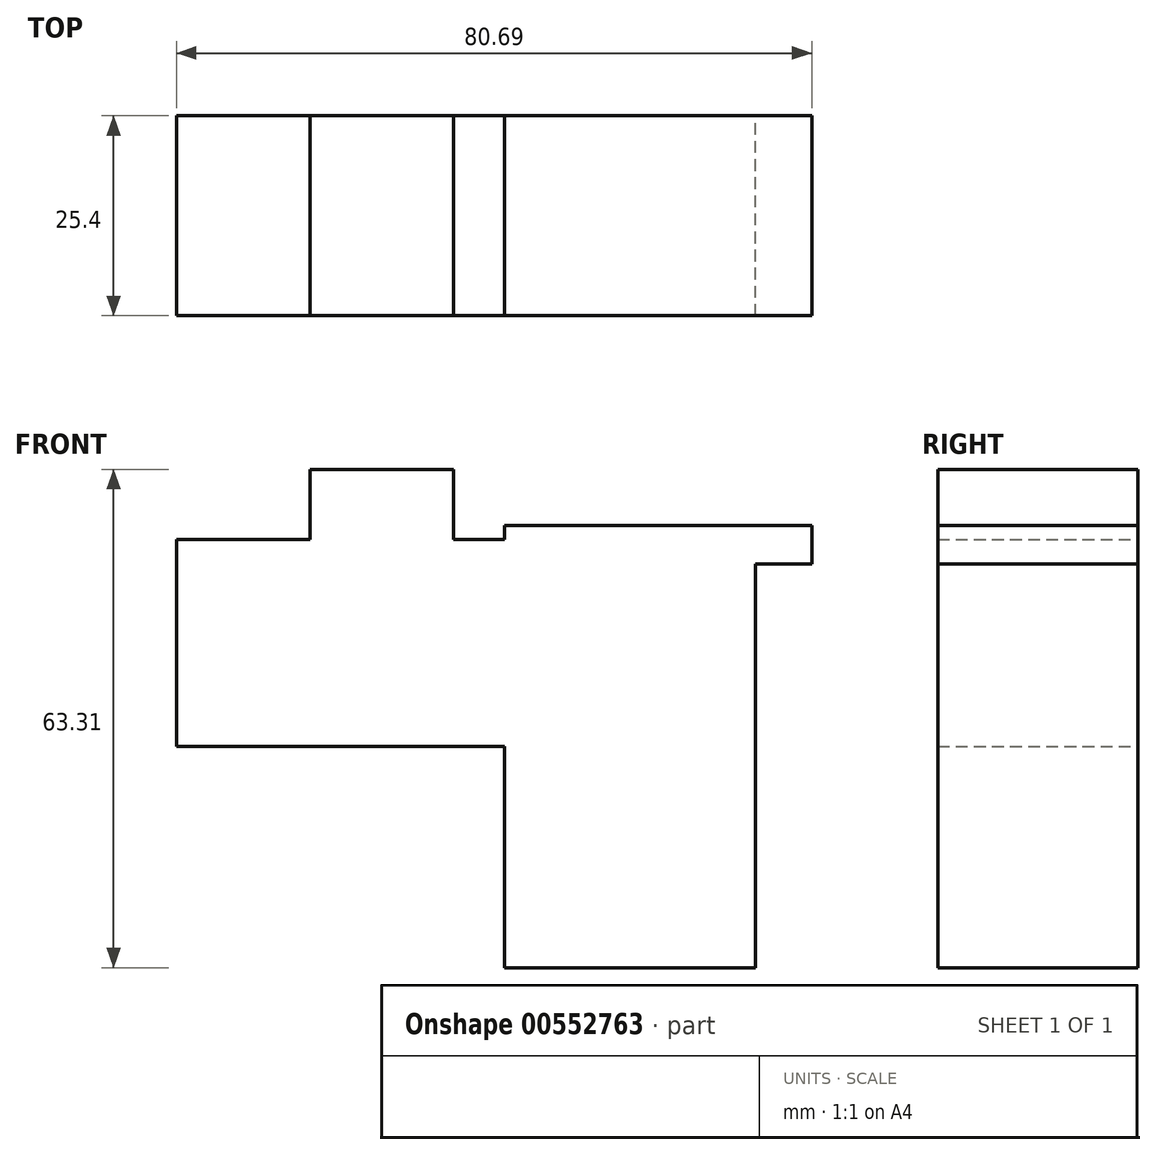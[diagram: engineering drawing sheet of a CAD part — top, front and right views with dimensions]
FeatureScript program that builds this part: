
annotation { "Feature Type Name" : "Feature", "Feature Type Description" : "" }
export const myFeature = defineFeature(function(context is Context, id is Id, definition is map)
    precondition{}
    {
        {
            var Q0;
            Q0=qCreatedBy(makeId("Front.planeOp"),FACE);
            var sketch = newSketch(context, id + "F0", { "sketchPlane" : qUnion([Q0])});
            skLineSegment(sketch, "E0.bottom", {"start": v(0, 0) * mm, "end": v(-41.68, 0) * mm});
            skLineSegment(sketch, "E0.top", {"start": v(0, 26.3) * mm, "end": v(-41.68, 26.3) * mm});
            skLineSegment(sketch, "E0.left", {"start": v(0, 0) * mm, "end": v(0, 26.3) * mm});
            skLineSegment(sketch, "E0.right", {"start": v(-41.68, 0) * mm, "end": v(-41.68, 26.3) * mm});
            skLineSegment(sketch, "E1.bottom", {"start": v(0, 0) * mm, "end": v(31.88, 0) * mm});
            skLineSegment(sketch, "E1.top", {"start": v(0, -28.09) * mm, "end": v(31.88, -28.09) * mm});
            skLineSegment(sketch, "E1.left", {"start": v(0, 0) * mm, "end": v(0, -28.09) * mm});
            skLineSegment(sketch, "E1.right", {"start": v(31.88, 0) * mm, "end": v(31.88, -28.09) * mm});
            skLineSegment(sketch, "E2.top", {"start": v(0, 28.09) * mm, "end": v(31.88, 28.09) * mm});
            skLineSegment(sketch, "E2.left", {"start": v(0, 0) * mm, "end": v(0, 28.09) * mm});
            skLineSegment(sketch, "E2.right", {"start": v(31.88, 0) * mm, "end": v(31.88, 28.09) * mm});
            skLineSegment(sketch, "E3.bottom", {"start": v(-41.68, 0) * mm, "end": v(0, 0) * mm});
            skLineSegment(sketch, "E3.top", {"start": v(-41.68, -28.09) * mm, "end": v(0, -28.09) * mm});
            skLineSegment(sketch, "E3.left", {"start": v(-41.68, 0) * mm, "end": v(-41.68, -28.09) * mm});
            skLineSegment(sketch, "E4.bottom", {"start": v(31.88, 28.09) * mm, "end": v(39, 28.09) * mm});
            skLineSegment(sketch, "E4.top", {"start": v(31.88, 23.18) * mm, "end": v(39, 23.18) * mm});
            skLineSegment(sketch, "E4.left", {"start": v(31.88, 28.09) * mm, "end": v(31.88, 23.18) * mm});
            skLineSegment(sketch, "E4.right", {"start": v(39, 28.09) * mm, "end": v(39, 23.18) * mm});
            skLineSegment(sketch, "E5.bottom", {"start": v(-24.74, 8.02) * mm, "end": v(-6.46, 8.02) * mm});
            skLineSegment(sketch, "E5.top", {"start": v(-24.74, 35.22) * mm, "end": v(-6.46, 35.22) * mm});
            skLineSegment(sketch, "E5.left", {"start": v(-24.74, 8.02) * mm, "end": v(-24.74, 35.22) * mm});
            skLineSegment(sketch, "E5.right", {"start": v(-6.46, 8.02) * mm, "end": v(-6.46, 35.22) * mm});
            skSolve(sketch);
        }
        {
            var Q0;
            {var subQ5=sQuery(id+"F0.wireOp",EDGE,"E5.top");Q0=makeQuery(id+"F0.imprint","IMPRINT",FACE,{"disambiguationData":[TD([[makeQuery(id+"F0.imprint","IMPRINT",EDGE,{"derivedFrom":subQ5}),-1.0]])]});}
            var Q1;
            Q1=makeQuery(id+"F0.imprint","IMPRINT",FACE,{"disambiguationData":[TD([[makeQuery(id+"F0.imprint","IMPRINT",EDGE,{"derivedFrom":sQuery(id+"F0.wireOp",EDGE,"E4.bottom")}),-1.0]])]});
            var Q2;
            {var subQ5=sQuery(id+"F0.wireOp",EDGE,"E5.bottom");Q2=makeQuery(id+"F0.imprint","IMPRINT",FACE,{"disambiguationData":[TD([[makeQuery(id+"F0.imprint","IMPRINT",EDGE,{"derivedFrom":subQ5}),1.0]])]});}
            var Q3;
            Q3=makeQuery(id+"F0.imprint","IMPRINT",FACE,{"disambiguationData":[TD([[makeQuery(id+"F0.imprint","IMPRINT",EDGE,{"derivedFrom":sQuery(id+"F0.wireOp",EDGE,"E3.bottom")}),-1.0]])]});
            var Q4;
            {var subQ5=sQuery(id+"F0.wireOp",EDGE,"E0.right");Q4=makeQuery(id+"F0.imprint","IMPRINT",FACE,{"disambiguationData":[TD([[makeQuery(id+"F0.imprint","IMPRINT",EDGE,{"derivedFrom":subQ5}),-1.0]])]});}
            var Q5;
            {var subQ3=sQuery(id+"F0.wireOp",EDGE,"E1.bottom");Q5=makeQuery(id+"F0.imprint","IMPRINT",FACE,{"disambiguationData":[TD([[makeQuery(id+"F0.imprint","IMPRINT",EDGE,{"derivedFrom":subQ3}),1.0]])]});}
            var Q6;
            Q6=makeQuery(id+"F0.imprint","IMPRINT",FACE,{"disambiguationData":[TD([[makeQuery(id+"F0.imprint","IMPRINT",EDGE,{"derivedFrom":sQuery(id+"F0.wireOp",EDGE,"E1.top")}),1.0]])]});
            extrude(context, id + "F1", {"entities" : qUnion([Q0, Q1, Q2, Q3, Q4, Q5, Q6]), "depth" : 25.4 * mm, "offsetDistance" : 25.4 * mm});
        }
    });
